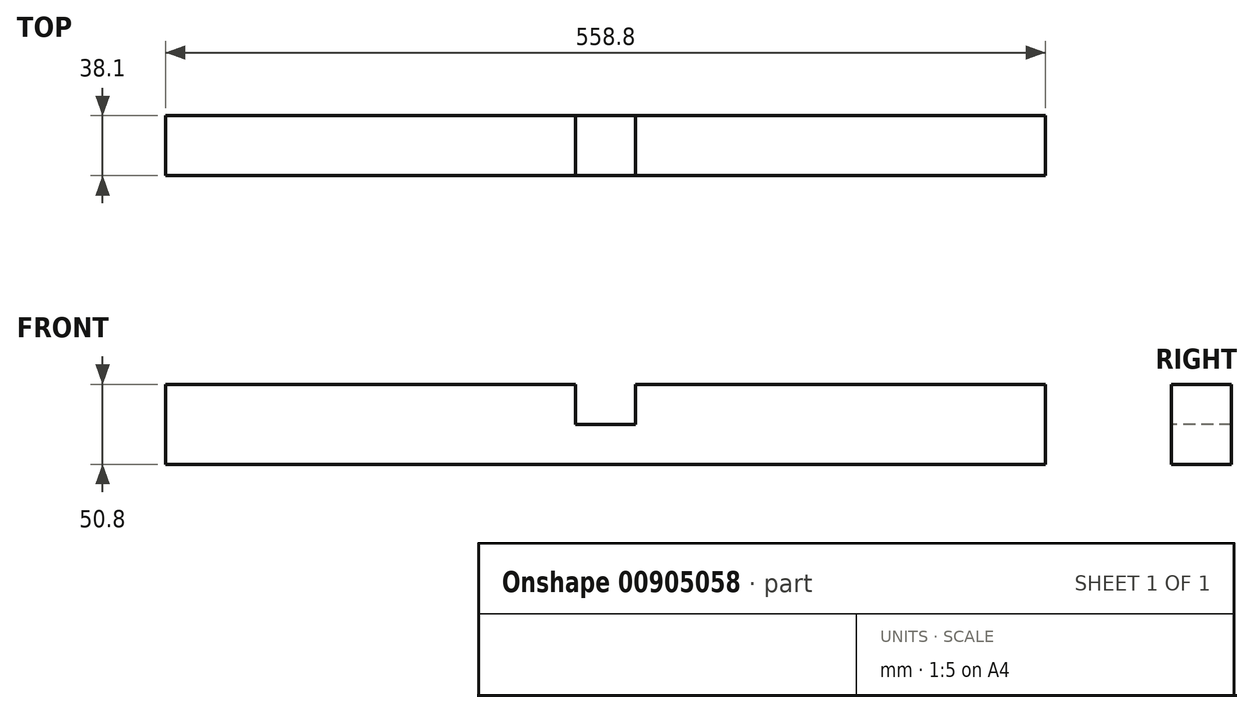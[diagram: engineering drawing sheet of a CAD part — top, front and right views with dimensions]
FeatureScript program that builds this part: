
annotation { "Feature Type Name" : "Feature", "Feature Type Description" : "" }
export const myFeature = defineFeature(function(context is Context, id is Id, definition is map)
    precondition{}
    {
        {
            var Q0;
            Q0=qCreatedBy(makeId("Top.planeOp"),FACE);
            var sketch = newSketch(context, id + "F0", { "sketchPlane" : qUnion([Q0])});
            skLineSegment(sketch, "E0.bottom", {"start": v(279.4, 19.05) * mm, "end": v(-279.4, 19.05) * mm});
            skLineSegment(sketch, "E0.top", {"start": v(279.4, -19.05) * mm, "end": v(-279.4, -19.05) * mm});
            skLineSegment(sketch, "E0.left", {"start": v(279.4, 19.05) * mm, "end": v(279.4, -19.05) * mm});
            skLineSegment(sketch, "E0.right", {"start": v(-279.4, 19.05) * mm, "end": v(-279.4, -19.05) * mm});
            skPoint(sketch, "E0.middle", {"position": v(0, 0) * mm});
            skSolve(sketch);
        }
        {
            var Q0;
            Q0 = qSketchRegion(id + "F0", true);
            extrude(context, id + "F1", {"entities" : qUnion([Q0]), "depth" : 50.8 * mm, "offsetDistance" : 25.4 * mm});
        }
        {
            var Q0;
            Q0=makeQuery(id+"F1.opExtrude","CAP_FACE",FACE,{"disambiguationData":[OSD([sQuery(id+"F0.wireOp",EDGE,"E0.bottom"),sQuery(id+"F0.wireOp",EDGE,"E0.top"),sQuery(id+"F0.wireOp",EDGE,"E0.left"),sQuery(id+"F0.wireOp",EDGE,"E0.right")])],"isStart":false});
            var sketch = newSketch(context, id + "F2", { "sketchPlane" : qUnion([Q0])});
            skLineSegment(sketch, "E1", {"start": v(-279.4, 0) * mm, "end": v(0, 0) * mm, "construction": true});
            skLineSegment(sketch, "E2.bottom", {"start": v(-19.05, 19.05) * mm, "end": v(19.05, 19.05) * mm});
            skLineSegment(sketch, "E2.top", {"start": v(-19.05, -19.05) * mm, "end": v(19.05, -19.05) * mm});
            skLineSegment(sketch, "E2.left", {"start": v(-19.05, 19.05) * mm, "end": v(-19.05, -19.05) * mm});
            skLineSegment(sketch, "E2.right", {"start": v(19.05, 19.05) * mm, "end": v(19.05, -19.05) * mm});
            skPoint(sketch, "E2.middle", {"position": v(0, 0) * mm});
            skSolve(sketch);
        }
        {
            var Q0;
            Q0=makeQuery(id+"F2.imprint","IMPRINT",FACE,{"disambiguationData":[TD([[makeQuery(id+"F2.imprint","IMPRINT",EDGE,{"derivedFrom":sQuery(id+"F2.wireOp",EDGE,"E2.bottom")}),1.0]])]});
            extrude(context, id + "F3", {"entities" : qUnion([Q0]), "operationType" : NewBodyOperationType.REMOVE, "oppositeDirection" : true, "depth" : 25.4 * mm, "offsetDistance" : 25.4 * mm});
        }
    });
